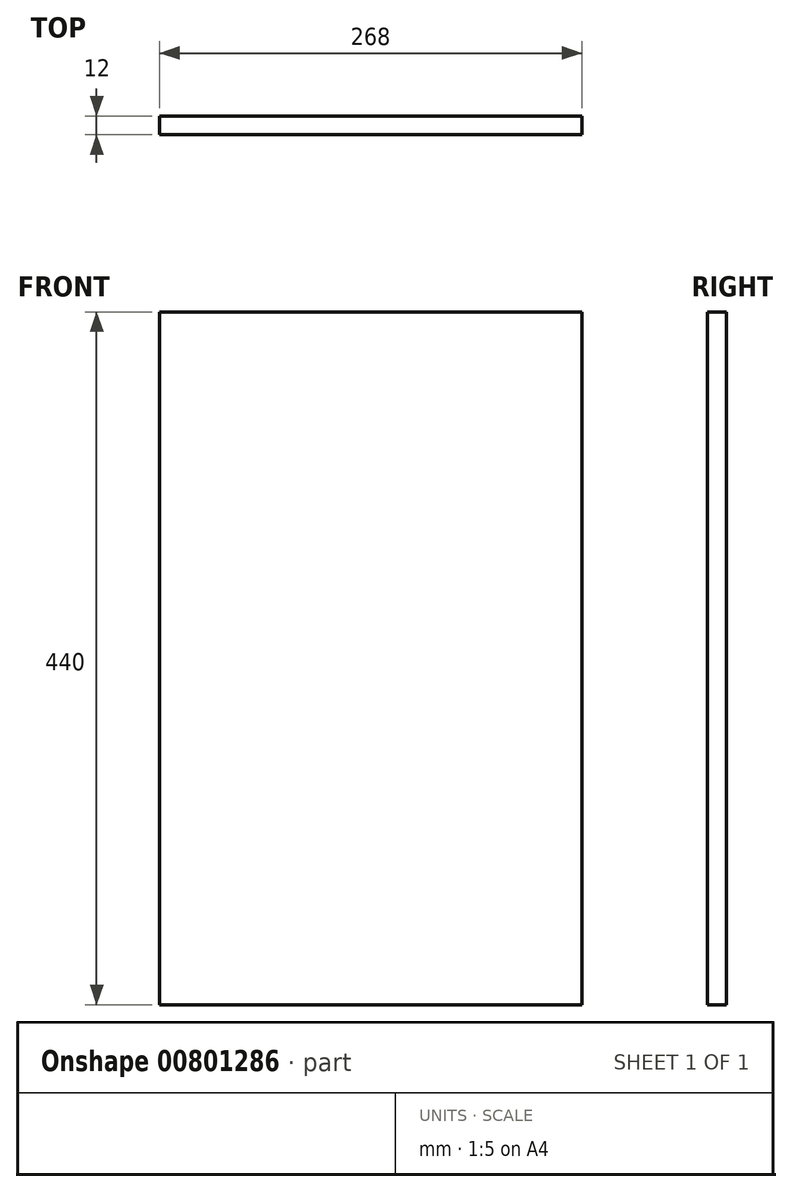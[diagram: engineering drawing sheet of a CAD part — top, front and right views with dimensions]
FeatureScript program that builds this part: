
annotation { "Feature Type Name" : "Feature", "Feature Type Description" : "" }
export const myFeature = defineFeature(function(context is Context, id is Id, definition is map)
    precondition{}
    {
        {
            var Q0;
            Q0=qCreatedBy(makeId("Front.planeOp"),FACE);
            var sketch = newSketch(context, id + "F0", { "sketchPlane" : qUnion([Q0])});
            skLineSegment(sketch, "E0.bottom", {"start": v(-134, -220) * mm, "end": v(134, -220) * mm});
            skLineSegment(sketch, "E0.top", {"start": v(-134, 220) * mm, "end": v(134, 220) * mm});
            skLineSegment(sketch, "E0.left", {"start": v(-134, -220) * mm, "end": v(-134, 220) * mm});
            skLineSegment(sketch, "E0.right", {"start": v(134, -220) * mm, "end": v(134, 220) * mm});
            skPoint(sketch, "E0.middle", {"position": v(0, 0) * mm});
            skSolve(sketch);
        }
        {
            var Q0;
            Q0=makeQuery(id+"F0.imprint","IMPRINT",FACE,{"disambiguationData":[TD([[makeQuery(id+"F0.imprint","IMPRINT",EDGE,{"derivedFrom":sQuery(id+"F0.wireOp",EDGE,"E0.bottom")}),1.0]])]});
            extrude(context, id + "F1", {"entities" : qUnion([Q0]), "depth" : 12 * mm, "offsetDistance" : 25 * mm});
        }
    });
